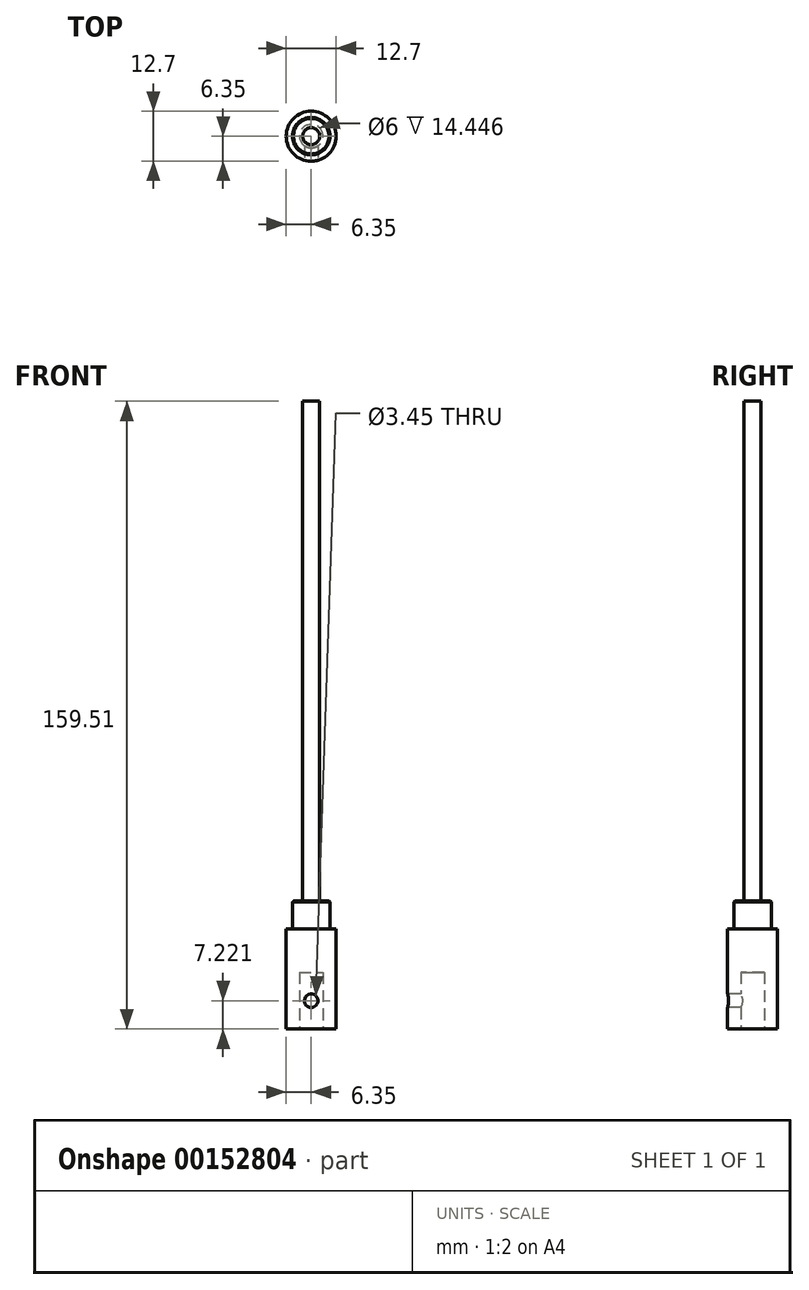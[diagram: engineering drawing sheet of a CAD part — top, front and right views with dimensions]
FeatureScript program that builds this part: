
annotation { "Feature Type Name" : "Feature", "Feature Type Description" : "" }
export const myFeature = defineFeature(function(context is Context, id is Id, definition is map)
    precondition{}
    {
        {
            var Q0;
            Q0=qCreatedBy(makeId("Top.planeOp"),FACE);
            var sketch = newSketch(context, id + "F0", { "sketchPlane" : qUnion([Q0])});
            skCircle(sketch, "E0", {"center": v(0, 0) * mm, "radius": 2.15 * mm});
            skSolve(sketch);
        }
        {
            var Q0;
            Q0=qSketchRegion(id+"F0",true);
            extrude(context, id + "F1", {"entities" : qUnion([Q0]), "depth" : 127 * mm});
        }
        {
            var Q0;
            Q0=makeQuery(id+"F1.opExtrude","CAP_FACE",FACE,{"disambiguationData":[OSD([sQuery(id+"F0.wireOp",EDGE,"E0")])],"isStart":true});
            var sketch = newSketch(context, id + "F2", { "sketchPlane" : qUnion([Q0])});
            skCircle(sketch, "E1", {"center": v(0, 0) * mm, "radius": 4.76 * mm});
            skSolve(sketch);
        }
        {
            var Q0;
            Q0=qSketchRegion(id+"F2",true);
            extrude(context, id + "F3", {"entities" : qUnion([Q0]), "operationType" : NewBodyOperationType.ADD, "depth" : 7.11 * mm});
        }
        {
            var Q0;
            Q0=makeQuery(id+"F3.opExtrude","CAP_FACE",FACE,{"disambiguationData":[OSD([sQuery(id+"F2.wireOp",EDGE,"E1")])],"isStart":false});
            var sketch = newSketch(context, id + "F4", { "sketchPlane" : qUnion([Q0])});
            skLineSegment(sketch, "E2.bottom", {"start": v(25.4, -25.4) * mm, "end": v(-25.4, -25.4) * mm});
            skLineSegment(sketch, "E2.top", {"start": v(25.4, 25.4) * mm, "end": v(-25.4, 25.4) * mm});
            skLineSegment(sketch, "E2.left", {"start": v(25.4, -25.4) * mm, "end": v(25.4, 25.4) * mm});
            skLineSegment(sketch, "E2.right", {"start": v(-25.4, -25.4) * mm, "end": v(-25.4, 25.4) * mm});
            skPoint(sketch, "E2.middle", {"position": v(0, 0) * mm});
            skCircle(sketch, "E3", {"center": v(0, 0) * mm, "radius": 3 * mm, "construction": true});
            skCircle(sketch, "E4", {"center": v(0, 0) * mm, "radius": 25.4 * mm, "construction": true});
            skLineSegment(sketch, "E5.bottom", {"start": v(7.76, 24.18) * mm, "end": v(3, 24.18) * mm, "construction": true});
            skLineSegment(sketch, "E5.top", {"start": v(7.76, -24.18) * mm, "end": v(3, -24.18) * mm, "construction": true});
            skLineSegment(sketch, "E5.left", {"start": v(7.76, 24.18) * mm, "end": v(7.76, -24.18) * mm, "construction": true});
            skLineSegment(sketch, "E5.right", {"start": v(3, 24.18) * mm, "end": v(3, -24.18) * mm, "construction": true});
            skSolve(sketch);
        }
        {
            var Q0;
            Q0=qSketchRegion(id+"F4",true);
            extrude(context, id + "F5", {"entities" : qUnion([Q0]), "operationType" : NewBodyOperationType.ADD, "depth" : 25.4 * mm});
        }
        {
            var Q0;
            Q0=makeQuery(id+"F5.opExtrude","CAP_FACE",FACE,{"disambiguationData":[OSD([sQuery(id+"F4.wireOp",EDGE,"E2.bottom"),sQuery(id+"F4.wireOp",EDGE,"E2.top"),sQuery(id+"F4.wireOp",EDGE,"E2.left"),sQuery(id+"F4.wireOp",EDGE,"E2.right")])],"isStart":false});
            var sketch = newSketch(context, id + "F6", { "sketchPlane" : qUnion([Q0])});
            skLineSegment(sketch, "E6", {"start": v(0, 25.4) * mm, "end": v(0, -25.4) * mm, "construction": true});
            skCircle(sketch, "E7", {"center": v(0, 0) * mm, "radius": 3 * mm});
            skSolve(sketch);
        }
        {
            var Q0;
            Q0=qSketchRegion(id+"F6",true);
            extrude(context, id + "F7", {"entities" : qUnion([Q0]), "operationType" : NewBodyOperationType.REMOVE, "oppositeDirection" : true, "depth" : 14.45 * mm});
        }
        {
            var Q0;
            Q0=makeQuery(id+"F5.opExtrude","SWEPT_FACE",FACE,{"disambiguationData":[OSD([sQuery(id+"F4.wireOp",EDGE,"E2.top")])]});
            var sketch = newSketch(context, id + "F8", { "sketchPlane" : qUnion([Q0])});
            skLineSegment(sketch, "E8", {"start": v(0, -18.07) * mm, "end": v(0, -32.51) * mm, "construction": true});
            skCircle(sketch, "E9", {"center": v(0, -25.29) * mm, "radius": 1.73 * mm});
            skSolve(sketch);
        }
        {
            var Q0;
            Q0=qSketchRegion(id+"F8",true);
            var Q1;
            Q1=makeQuery(id+"F7.boolean.opBoolean","COPY",FACE,{"derivedFrom":makeQuery(id+"F7.opExtrude","SWEPT_FACE",FACE,{"disambiguationData":[OSD([sQuery(id+"F6.wireOp",EDGE,"E7")])]})});
            extrude(context, id + "F9", {"entities" : qUnion([Q0]), "operationType" : NewBodyOperationType.REMOVE, "endBound" : BoundingType.UP_TO_SURFACE, "oppositeDirection" : true, "endBoundEntityFace" : qUnion([Q1]), "depth" : 25.4 * mm});
        }
        {
            var Q0;
            Q0=makeQuery(id+"F5.opExtrude","CAP_FACE",FACE,{"disambiguationData":[OSD([sQuery(id+"F4.wireOp",EDGE,"E2.bottom"),sQuery(id+"F4.wireOp",EDGE,"E2.top"),sQuery(id+"F4.wireOp",EDGE,"E2.left"),sQuery(id+"F4.wireOp",EDGE,"E2.right")])],"isStart":false});
            var sketch = newSketch(context, id + "F10", { "sketchPlane" : qUnion([Q0])});
            skLineSegment(sketch, "E10.bottom", {"start": v(-25.4, 25.4) * mm, "end": v(25.4, 25.4) * mm});
            skLineSegment(sketch, "E10.top", {"start": v(-25.4, -25.4) * mm, "end": v(25.4, -25.4) * mm});
            skLineSegment(sketch, "E10.left", {"start": v(-25.4, 25.4) * mm, "end": v(-25.4, -25.4) * mm});
            skLineSegment(sketch, "E10.right", {"start": v(25.4, 25.4) * mm, "end": v(25.4, -25.4) * mm});
            skPoint(sketch, "E10.middle", {"position": v(0, 0) * mm});
            skCircle(sketch, "E11", {"center": v(0, 0) * mm, "radius": 6.35 * mm});
            skSolve(sketch);
        }
        {
            var Q0;
            Q0=qSketchRegion(id+"F10",true);
            var Q1;
            Q1=makeQuery(id+"F5.opExtrude","CAP_FACE",FACE,{"disambiguationData":[OSD([sQuery(id+"F4.wireOp",EDGE,"E2.bottom"),sQuery(id+"F4.wireOp",EDGE,"E2.top"),sQuery(id+"F4.wireOp",EDGE,"E2.left"),sQuery(id+"F4.wireOp",EDGE,"E2.right")])],"isStart":true});
            extrude(context, id + "F11", {"entities" : qUnion([Q0]), "operationType" : NewBodyOperationType.REMOVE, "endBound" : BoundingType.UP_TO_SURFACE, "oppositeDirection" : true, "endBoundEntityFace" : qUnion([Q1]), "depth" : 25.4 * mm});
        }
        {
            var Q0;
            Q0=makeQuery(id+"F3.opExtrude","CAP_EDGE",EDGE,{"disambiguationData":[OSD([sQuery(id+"F2.wireOp",EDGE,"E1")])],"isStart":true});
            chamfer(context, id + "F12", {"entities" : qUnion([Q0]), "width" : 0.25 * mm, "tangentPropagation" : true});
        }
    });
